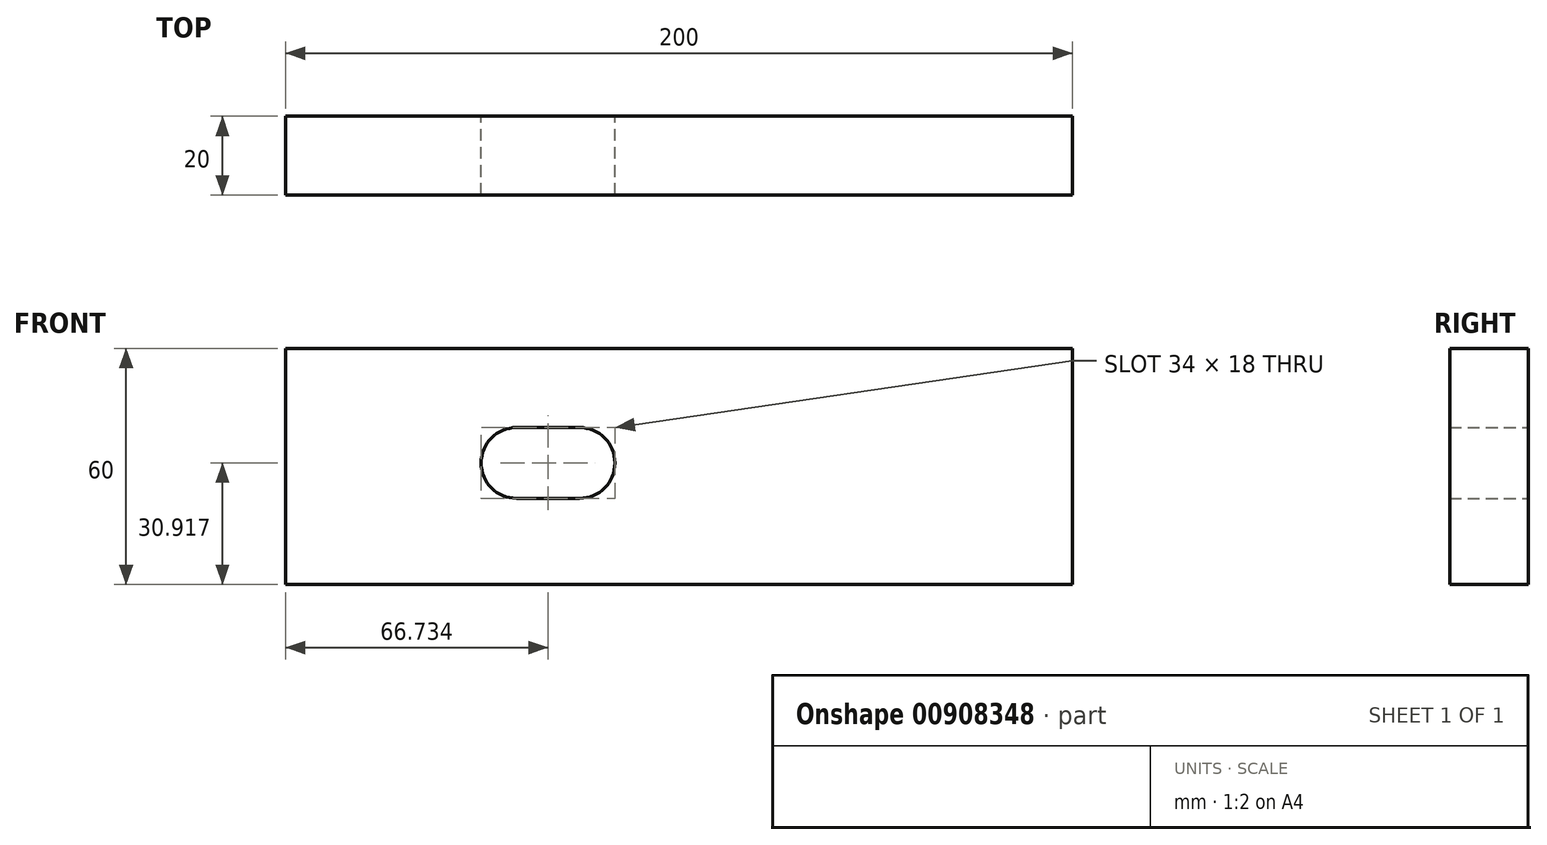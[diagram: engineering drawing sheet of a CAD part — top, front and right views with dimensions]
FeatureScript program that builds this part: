
annotation { "Feature Type Name" : "Feature", "Feature Type Description" : "" }
export const myFeature = defineFeature(function(context is Context, id is Id, definition is map)
    precondition{}
    {
        {
            var Q0;
            Q0=qCreatedBy(makeId("Front.planeOp"),FACE);
            var sketch = newSketch(context, id + "F0", { "sketchPlane" : qUnion([Q0])});
            skLineSegment(sketch, "E0.bottom", {"start": v(-112.35, 4.02) * mm, "end": v(87.65, 4.02) * mm});
            skLineSegment(sketch, "E0.top", {"start": v(-112.35, -55.98) * mm, "end": v(87.65, -55.98) * mm});
            skLineSegment(sketch, "E0.left", {"start": v(-112.35, 4.02) * mm, "end": v(-112.35, -55.98) * mm});
            skLineSegment(sketch, "E0.right", {"start": v(87.65, 4.02) * mm, "end": v(87.65, -55.98) * mm});
            skLineSegment(sketch, "E1", {"start": v(-37.62, -16.06) * mm, "end": v(-53.62, -16.06) * mm});
            skLineSegment(sketch, "E2", {"start": v(-37.62, -34.06) * mm, "end": v(-53.62, -34.06) * mm});
            skArc(sketch, "E3", {"start": v(-53.62, -16.06) * mm, "mid": v(-62.62, -25.06) * mm, "end": v(-53.62, -34.06) * mm});
            skArc(sketch, "E4", {"start": v(-37.62, -34.06) * mm, "mid": v(-28.62, -25.06) * mm, "end": v(-37.62, -16.06) * mm});
            skSolve(sketch);
        }
        {
            var Q0;
            Q0 = qSketchRegion(id + "F0", true);
            var Q1;
            Q1=makeQuery(id+"F0.imprint","IMPRINT",FACE,{"disambiguationData":[TD([[makeQuery(id+"F0.imprint","IMPRINT",EDGE,{"derivedFrom":sQuery(id+"F0.wireOp",EDGE,"E0.bottom")}),-1.0]])]});
            extrude(context, id + "F1", {"entities" : qUnion([Q0, Q1]), "depth" : 20 * mm, "offsetDistance" : 25 * mm});
        }
    });
